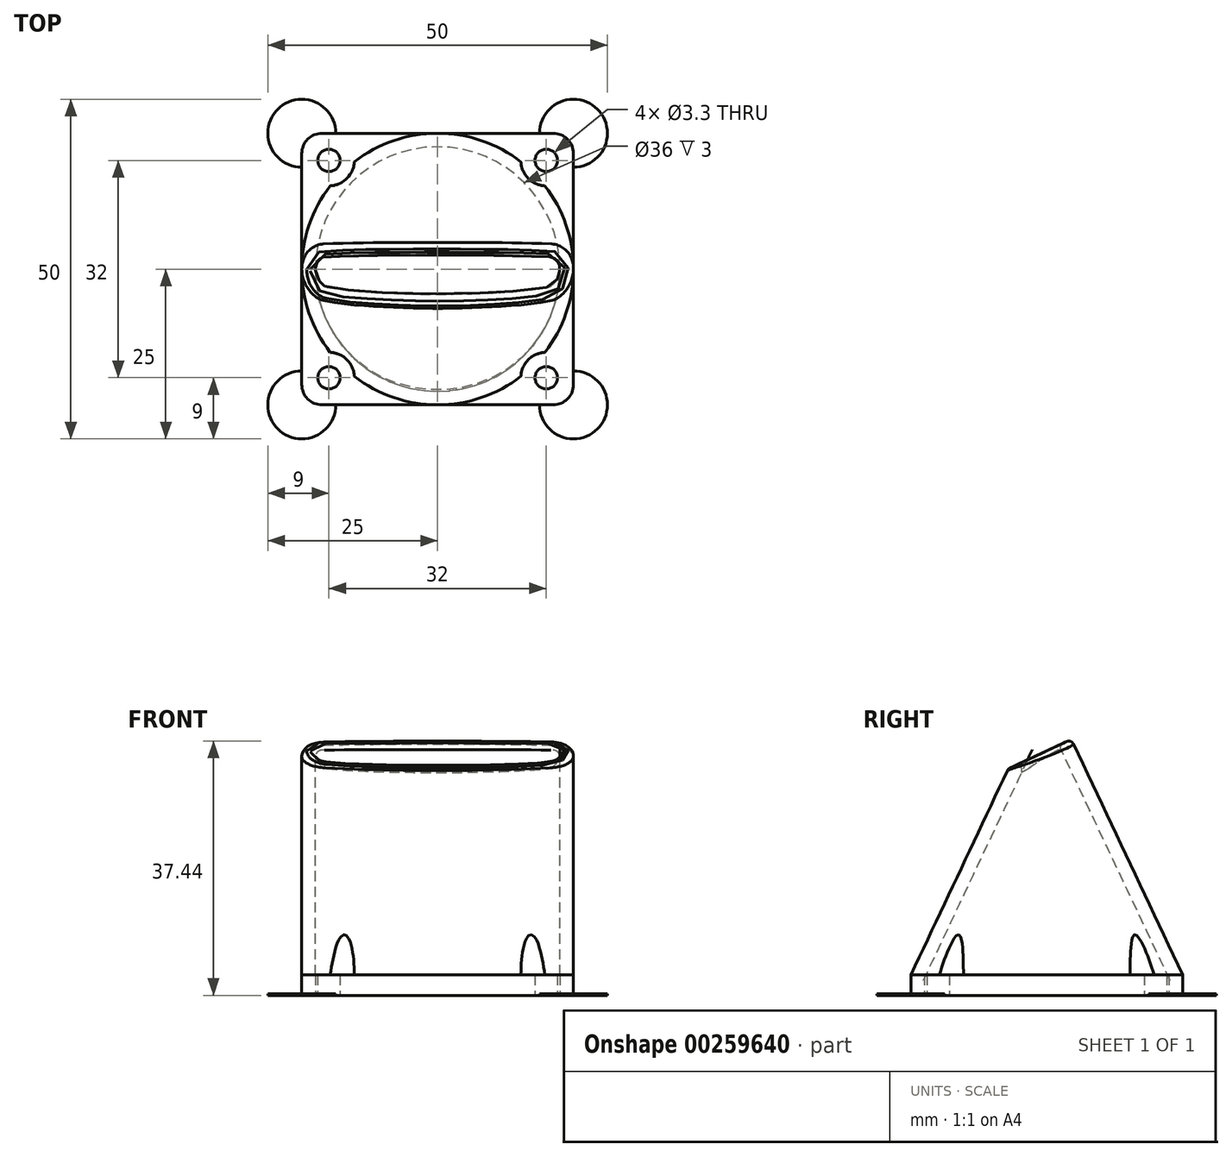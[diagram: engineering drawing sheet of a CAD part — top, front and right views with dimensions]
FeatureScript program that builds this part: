
annotation { "Feature Type Name" : "Feature", "Feature Type Description" : "" }
export const myFeature = defineFeature(function(context is Context, id is Id, definition is map)
    precondition{}
    {
        {
            var Q0;
            Q0=qCreatedBy(makeId("Top.planeOp"),FACE);
            var sketch = newSketch(context, id + "F0", { "sketchPlane" : qUnion([Q0])});
            skLineSegment(sketch, "E0.bottom", {"start": v(3, 0) * mm, "end": v(37, 0) * mm});
            skLineSegment(sketch, "E0.top", {"start": v(3, -40) * mm, "end": v(37, -40) * mm});
            skLineSegment(sketch, "E0.left", {"start": v(0, -3) * mm, "end": v(0, -37) * mm});
            skLineSegment(sketch, "E0.right", {"start": v(40, -3) * mm, "end": v(40, -37) * mm});
            skLineSegment(sketch, "E1", {"start": v(0, 0) * mm, "end": v(40, -40) * mm, "construction": true});
            skLineSegment(sketch, "E2", {"start": v(0, -40) * mm, "end": v(40, 0) * mm, "construction": true});
            skLineSegment(sketch, "E3", {"start": v(20, 0) * mm, "end": v(20, -40) * mm, "construction": true});
            skCircle(sketch, "E4", {"center": v(20, -20) * mm, "radius": 18 * mm});
            skCircle(sketch, "E5", {"center": v(4, -4) * mm, "radius": 1.65 * mm});
            skCircle(sketch, "E6", {"center": v(36, -4) * mm, "radius": 1.65 * mm});
            skCircle(sketch, "E7", {"center": v(36, -36) * mm, "radius": 1.65 * mm});
            skCircle(sketch, "E8", {"center": v(4, -36) * mm, "radius": 1.65 * mm});
            skPoint(sketch, "E9.visualSharp", {"position": v(0, -40) * mm});
            skArc(sketch, "E9.filletArc", {"start": v(0, -37) * mm, "mid": v(0.88, -39.12) * mm, "end": v(3, -40) * mm});
            skPoint(sketch, "E10.visualSharp", {"position": v(40, -40) * mm});
            skArc(sketch, "E10.filletArc", {"start": v(37, -40) * mm, "mid": v(39.12, -39.12) * mm, "end": v(40, -37) * mm});
            skPoint(sketch, "E11.visualSharp", {"position": v(40, 0) * mm});
            skArc(sketch, "E11.filletArc", {"start": v(40, -3) * mm, "mid": v(39.12, -0.88) * mm, "end": v(37, 0) * mm});
            skPoint(sketch, "E12.visualSharp", {"position": v(0, 0) * mm});
            skArc(sketch, "E12.filletArc", {"start": v(3, 0) * mm, "mid": v(0.88, -0.88) * mm, "end": v(0, -3) * mm});
            skSolve(sketch);
        }
        {
            var Q0;
            Q0=qSketchRegion(id+"F0",true);
            extrude(context, id + "F1", {"entities" : qUnion([Q0]), "depth" : 3 * mm});
        }
        {
            var Q0;
            Q0=makeQuery(id+"F1.opExtrude","CAP_FACE",FACE,{"disambiguationData":[OSD([sQuery(id+"F0.wireOp",EDGE,"E0.bottom"),sQuery(id+"F0.wireOp",EDGE,"E0.top"),sQuery(id+"F0.wireOp",EDGE,"E0.left"),sQuery(id+"F0.wireOp",EDGE,"E0.right"),sQuery(id+"F0.wireOp",EDGE,"E4"),sQuery(id+"F0.wireOp",EDGE,"E5"),sQuery(id+"F0.wireOp",EDGE,"E6"),sQuery(id+"F0.wireOp",EDGE,"E7"),sQuery(id+"F0.wireOp",EDGE,"E8"),sQuery(id+"F0.wireOp",EDGE,"E9.filletArc"),sQuery(id+"F0.wireOp",EDGE,"E10.filletArc"),sQuery(id+"F0.wireOp",EDGE,"E11.filletArc"),sQuery(id+"F0.wireOp",EDGE,"E12.filletArc")])],"isStart":false});
            var sketch = newSketch(context, id + "F2", { "sketchPlane" : qUnion([Q0])});
            skLineSegment(sketch, "E13", {"start": v(0, 0) * mm, "end": v(20, -20) * mm, "construction": true});
            skLineSegment(sketch, "E14", {"start": v(4, -36) * mm, "end": v(36, -4) * mm, "construction": true});
            skLineSegment(sketch, "E15", {"start": v(20, -20) * mm, "end": v(36, -36) * mm, "construction": true});
            skArc(sketch, "E16", {"start": v(5.86, -5.86) * mm, "mid": v(1.52, -12.35) * mm, "end": v(0, -20) * mm});
            skArc(sketch, "E17", {"start": v(5.86, -34.14) * mm, "mid": v(20, -40) * mm, "end": v(34.14, -34.14) * mm});
            skArc(sketch, "E18", {"start": v(34.14, -5.86) * mm, "mid": v(20, 0) * mm, "end": v(5.86, -5.86) * mm});
            skArc(sketch, "E19", {"start": v(34.14, -34.14) * mm, "mid": v(38.48, -27.65) * mm, "end": v(40, -20) * mm});
            skLineSegment(sketch, "E20", {"start": v(0, -20) * mm, "end": v(40, -20) * mm, "construction": true});
            skArc(sketch, "E21", {"start": v(0, -20) * mm, "mid": v(1.52, -27.65) * mm, "end": v(5.86, -34.14) * mm});
            skArc(sketch, "E22", {"start": v(40, -20) * mm, "mid": v(38.48, -12.35) * mm, "end": v(34.14, -5.86) * mm});
            skSolve(sketch);
        }
        {
            var Q0;
            Q0=makeQuery(id+"F2.imprint","IMPRINT",FACE,{"disambiguationData":[TD([[makeQuery(id+"F2.imprint","IMPRINT",EDGE,{"derivedFrom":makeQuery(id+"F1.opExtrude","CAP_EDGE",EDGE,{"disambiguationData":[OSD([sQuery(id+"F0.wireOp",EDGE,"E6")])],"isStart":false})}),-1.0]])]});
            cPlane(context, id + "F3", {"entities" : qUnion([Q0]), "cplaneType" : CPlaneType.OFFSET, "offset" : 36 * mm, "width" : 150 * mm, "height" : 150 * mm});
        }
        {
            var Q0;
            Q0=qCreatedBy(id+"F3.planeOp",FACE);
            var sketch = newSketch(context, id + "F4", { "sketchPlane" : qUnion([Q0])});
            skLineSegment(sketch, "E23", {"start": v(20, -20) * mm, "end": v(40, -20) * mm, "construction": true});
            skArc(sketch, "E24", {"start": v(3, -17) * mm, "mid": v(0.88, -17.88) * mm, "end": v(0, -20) * mm});
            skArc(sketch, "E25", {"start": v(37, -23) * mm, "mid": v(39.12, -22.12) * mm, "end": v(40, -20) * mm});
            skLineSegment(sketch, "E26", {"start": v(3, -17) * mm, "end": v(37, -17) * mm});
            skLineSegment(sketch, "E27", {"start": v(3, -23) * mm, "end": v(37, -23) * mm});
            skLineSegment(sketch, "E28", {"start": v(0, 0) * mm, "end": v(20, -20) * mm, "construction": true});
            skLineSegment(sketch, "E29", {"start": v(0, -20) * mm, "end": v(20, -20) * mm, "construction": true});
            skArc(sketch, "E30", {"start": v(0, -20) * mm, "mid": v(0.88, -22.12) * mm, "end": v(3, -23) * mm});
            skArc(sketch, "E31", {"start": v(40, -20) * mm, "mid": v(39.12, -17.88) * mm, "end": v(37, -17) * mm});
            skSolve(sketch);
        }
        {
            var Q0;
            Q0=makeQuery(id+"F1.opExtrude","SWEPT_FACE",FACE,{"disambiguationData":[OSD([sQuery(id+"F0.wireOp",EDGE,"E0.top")])]});
            cPlane(context, id + "F5", {"entities" : qUnion([Q0]), "cplaneType" : CPlaneType.OFFSET, "offset" : 20 * mm, "oppositeDirection" : true, "width" : 150 * mm, "height" : 150 * mm});
        }
        {
            var Q0;
            Q0=qCreatedBy(id+"F5.planeOp",FACE);
            var sketch = newSketch(context, id + "F6", { "sketchPlane" : qUnion([Q0])});
            skLineSegment(sketch, "E32", {"start": v(0, 0) * mm, "end": v(0, 3) * mm, "construction": true});
            skLineSegment(sketch, "E33", {"start": v(0, 3) * mm, "end": v(0, 39) * mm});
            skLineSegment(sketch, "E34", {"start": v(0, 0) * mm, "end": v(40, 0) * mm, "construction": true});
            skLineSegment(sketch, "E35", {"start": v(40, 0) * mm, "end": v(40, 3) * mm, "construction": true});
            skLineSegment(sketch, "E36", {"start": v(40, 3) * mm, "end": v(40, 39) * mm});
            skSolve(sketch);
        }
        {
            var Q0;
            Q0=makeQuery(id+"F1.opExtrude","SWEPT_FACE",FACE,{"disambiguationData":[OSD([sQuery(id+"F0.wireOp",EDGE,"E0.right")])]});
            cPlane(context, id + "F7", {"entities" : qUnion([Q0]), "cplaneType" : CPlaneType.OFFSET, "offset" : 20 * mm, "oppositeDirection" : true, "width" : 150 * mm, "height" : 150 * mm});
        }
        {
            var Q0;
            Q0=qCreatedBy(id+"F7.planeOp",FACE);
            var sketch = newSketch(context, id + "F8", { "sketchPlane" : qUnion([Q0])});
            skLineSegment(sketch, "E37", {"start": v(0, 0) * mm, "end": v(0, 3) * mm, "construction": true});
            skLineSegment(sketch, "E38", {"start": v(0, 3) * mm, "end": v(-40, 3) * mm, "construction": true});
            skLineSegment(sketch, "E39", {"start": v(0, 3) * mm, "end": v(0, 39) * mm, "construction": true});
            skLineSegment(sketch, "E40", {"start": v(0, 39) * mm, "end": v(-17, 39) * mm, "construction": true});
            skLineSegment(sketch, "E41", {"start": v(-17, 39) * mm, "end": v(-23, 39) * mm, "construction": true});
            skLineSegment(sketch, "E42", {"start": v(-23, 39) * mm, "end": v(-23, 42) * mm, "construction": true});
            skLineSegment(sketch, "E43", {"start": v(-40, 3) * mm, "end": v(-40, 0) * mm, "construction": true});
            skLineSegment(sketch, "E44", {"start": v(-23, 39) * mm, "end": v(-40, 3) * mm});
            skLineSegment(sketch, "E45", {"start": v(-17, 39) * mm, "end": v(0, 3) * mm});
            skSolve(sketch);
        }
        {
            var Q1;
            Q1=qSketchRegion(id+"F2",true);
            var Q2;
            Q2=qSketchRegion(id+"F4",true);
            var Q3;
            Q3=sQuery(id+"F6.wireOp",EDGE,"E36");
            var Q4;
            Q4=sQuery(id+"F6.wireOp",EDGE,"E33");
            var Q5;
            Q5=sQuery(id+"F8.wireOp",EDGE,"E44");
            var Q6;
            Q6=sQuery(id+"F8.wireOp",EDGE,"E45");
            loft(context, id + "F9", {"addGuides" : true, "sheetProfilesArray" : [{ "sheetProfileEntities" : qUnion([Q1]) }, { "sheetProfileEntities" : qUnion([Q2]) }], "guidesArray" : [{ "guideEntities" : qUnion([Q3]), "guideDerivativeType" : LoftGuideDerivativeType.DEFAULT, "guideDerivativeMagnitude" : 1 }, { "guideEntities" : qUnion([Q4]), "guideDerivativeType" : LoftGuideDerivativeType.DEFAULT, "guideDerivativeMagnitude" : 1 }, { "guideEntities" : qUnion([Q5]), "guideDerivativeType" : LoftGuideDerivativeType.DEFAULT, "guideDerivativeMagnitude" : 1 }, { "guideEntities" : qUnion([Q6]), "guideDerivativeType" : LoftGuideDerivativeType.DEFAULT, "guideDerivativeMagnitude" : 1 }]});
        }
        {
            var Q0;
            Q0=makeQuery(id+"F9.opLoft","CAP_FACE",FACE,{"disambiguationData":[OSD([makeQuery(id+"F4.imprint","IMPRINT",FACE,{"disambiguationData":[TD([[makeQuery(id+"F4.imprint","IMPRINT",EDGE,{"derivedFrom":sQuery(id+"F4.wireOp",EDGE,"E24")}),1.0]])]})])],"isStart":true});
            var Q1;
            {var subQ7=sQuery(id+"F2.wireOp",EDGE,"E16");Q1=makeQuery(id+"F9.opLoft","CAP_FACE",FACE,{"disambiguationData":[OSD([makeQuery(id+"F2.imprint","IMPRINT",FACE,{"disambiguationData":[TD([[makeQuery(id+"F2.imprint","IMPRINT",EDGE,{"derivedFrom":subQ7}),1.0]])]})])],"isStart":true});}
            shell(context, id + "F10", {"entities" : qUnion([Q0, Q1]), "thickness" : 2 * mm});
        }
        {
            var Q0;
            Q0=makeQuery(id+"F1.opExtrude","SWEPT_BODY",BODY,{"disambiguationData":[OSD([sQuery(id+"F0.wireOp",EDGE,"E0.bottom"),sQuery(id+"F0.wireOp",EDGE,"E0.top"),sQuery(id+"F0.wireOp",EDGE,"E0.left"),sQuery(id+"F0.wireOp",EDGE,"E0.right"),sQuery(id+"F0.wireOp",EDGE,"E4"),sQuery(id+"F0.wireOp",EDGE,"E5"),sQuery(id+"F0.wireOp",EDGE,"E6"),sQuery(id+"F0.wireOp",EDGE,"E7"),sQuery(id+"F0.wireOp",EDGE,"E8"),sQuery(id+"F0.wireOp",EDGE,"E9.filletArc"),sQuery(id+"F0.wireOp",EDGE,"E10.filletArc"),sQuery(id+"F0.wireOp",EDGE,"E11.filletArc"),sQuery(id+"F0.wireOp",EDGE,"E12.filletArc")])]});
            var Q1;
            Q1=makeQuery(id+"F9.opLoft","SWEPT_BODY",BODY,{"disambiguationData":[OSD([makeQuery(id+"F2.imprint","IMPRINT",FACE,{"disambiguationData":[TD([[makeQuery(id+"F2.imprint","IMPRINT",EDGE,{"derivedFrom":makeQuery(id+"F1.opExtrude","CAP_EDGE",EDGE,{"disambiguationData":[OSD([sQuery(id+"F0.wireOp",EDGE,"E4")])],"isStart":false})}),1.0]])]}),makeQuery(id+"F4.imprint","IMPRINT",FACE,{"disambiguationData":[TD([[makeQuery(id+"F4.imprint","IMPRINT",EDGE,{"derivedFrom":sQuery(id+"F4.wireOp",EDGE,"E24")}),1.0]])]}),sQuery(id+"F6.wireOp",EDGE,"E33"),sQuery(id+"F6.wireOp",EDGE,"E36")])]});
            booleanBodies(context, id + "F11", {"operationType" : BooleanOperationType.UNION, "tools" : qUnion([Q0, Q1])});
        }
        {
            var Q0;
            Q0=qCreatedBy(makeId("Right.planeOp"),FACE);
            var sketch = newSketch(context, id + "F12", { "sketchPlane" : qUnion([Q0])});
            skLineSegment(sketch, "E46", {"start": v(0, 0) * mm, "end": v(-20, 0) * mm, "construction": true});
            skLineSegment(sketch, "E47", {"start": v(-20, 0) * mm, "end": v(-20, 36) * mm, "construction": true});
            skLineSegment(sketch, "E48", {"start": v(-20, 36) * mm, "end": v(-1.87, 44.45) * mm});
            skLineSegment(sketch, "E49", {"start": v(-1.87, 44.45) * mm, "end": v(-6.95, 55.33) * mm});
            skLineSegment(sketch, "E50", {"start": v(-6.95, 55.33) * mm, "end": v(-43.2, 38.42) * mm});
            skLineSegment(sketch, "E51", {"start": v(-43.2, 38.42) * mm, "end": v(-38.13, 27.55) * mm});
            skLineSegment(sketch, "E52", {"start": v(-38.13, 27.55) * mm, "end": v(-20, 36) * mm});
            skSolve(sketch);
        }
        {
            var Q0;
            Q0=qSketchRegion(id+"F12",true);
            extrude(context, id + "F13", {"entities" : qUnion([Q0]), "operationType" : NewBodyOperationType.REMOVE, "endBound" : BoundingType.THROUGH_ALL, "depth" : 25 * mm});
        }
        {
            var Q0;
            Q0=makeQuery(id+"F13.boolean.opBoolean","INTERSECT",EDGE,{"derivedFrom":[makeQuery(id+"F10.opShell","OFFSET_FACE",FACE,{"disambiguationData":[OSD([sQuery(id+"F2.wireOp",EDGE,"E16"),sQuery(id+"F2.wireOp",EDGE,"E17"),sQuery(id+"F2.wireOp",EDGE,"E21"),sQuery(id+"F4.wireOp",EDGE,"E30"),sQuery(id+"F6.wireOp",EDGE,"E33")])]}),makeQuery(id+"F13.opExtrude","SWEPT_FACE",FACE,{"disambiguationData":[OSD([sQuery(id+"F12.wireOp",EDGE,"E48"),sQuery(id+"F12.wireOp",EDGE,"E52")])]})]});
            var Q1;
            Q1=makeQuery(id+"F13.boolean.opBoolean","INTERSECT",EDGE,{"derivedFrom":[makeQuery(id+"F9.opLoft","SWEPT_FACE",FACE,{"disambiguationData":[OSD([sQuery(id+"F2.wireOp",EDGE,"E16"),sQuery(id+"F2.wireOp",EDGE,"E17"),sQuery(id+"F2.wireOp",EDGE,"E21"),sQuery(id+"F4.wireOp",EDGE,"E30"),sQuery(id+"F6.wireOp",EDGE,"E33")])]}),makeQuery(id+"F13.opExtrude","SWEPT_FACE",FACE,{"disambiguationData":[OSD([sQuery(id+"F12.wireOp",EDGE,"E48"),sQuery(id+"F12.wireOp",EDGE,"E52")])]})]});
            fillet(context, id + "F14", {"entities" : qUnion([Q0, Q1]), "radius" : 0.75 * mm, "tangentPropagation" : true, "allowEdgeOverflow" : false});
        }
        {
            var Q0;
            Q0=qCreatedBy(makeId("Top.planeOp"),FACE);
            var sketch = newSketch(context, id + "F15", { "sketchPlane" : qUnion([Q0])});
            skLineSegment(sketch, "E53.bottom", {"start": v(0, 0) * mm, "end": v(40, 0) * mm, "construction": true});
            skLineSegment(sketch, "E53.top", {"start": v(0, -40) * mm, "end": v(40, -40) * mm, "construction": true});
            skLineSegment(sketch, "E53.left", {"start": v(0, 0) * mm, "end": v(0, -40) * mm, "construction": true});
            skLineSegment(sketch, "E53.right", {"start": v(40, 0) * mm, "end": v(40, -40) * mm, "construction": true});
            skLineSegment(sketch, "E54", {"start": v(0, 0) * mm, "end": v(40, -40) * mm, "construction": true});
            skLineSegment(sketch, "E55", {"start": v(0, -40) * mm, "end": v(40, 0) * mm, "construction": true});
            skLineSegment(sketch, "E56", {"start": v(20, 0) * mm, "end": v(20, -40) * mm, "construction": true});
            skArc(sketch, "E57", {"start": v(4.39, -2.4) * mm, "mid": v(2.83, -2.83) * mm, "end": v(2.4, -4.39) * mm});
            skArc(sketch, "E58", {"start": v(4.39, -2.4) * mm, "mid": v(-3.54, 3.54) * mm, "end": v(2.4, -4.39) * mm});
            skArc(sketch, "E59", {"start": v(37.6, -4.39) * mm, "mid": v(37.17, -2.83) * mm, "end": v(35.61, -2.4) * mm});
            skArc(sketch, "E60", {"start": v(37.6, -4.39) * mm, "mid": v(43.54, 3.54) * mm, "end": v(35.61, -2.4) * mm});
            skArc(sketch, "E61", {"start": v(35.61, -37.6) * mm, "mid": v(43.54, -43.54) * mm, "end": v(37.6, -35.61) * mm});
            skArc(sketch, "E62", {"start": v(35.61, -37.6) * mm, "mid": v(37.17, -37.17) * mm, "end": v(37.6, -35.61) * mm});
            skArc(sketch, "E63", {"start": v(2.4, -35.61) * mm, "mid": v(-3.54, -43.54) * mm, "end": v(4.39, -37.6) * mm});
            skArc(sketch, "E64", {"start": v(2.4, -35.61) * mm, "mid": v(2.83, -37.17) * mm, "end": v(4.39, -37.6) * mm});
            skSolve(sketch);
        }
        {
            var Q0;
            Q0=qSketchRegion(id+"F15",true);
            extrude(context, id + "F16", {"entities" : qUnion([Q0]), "operationType" : NewBodyOperationType.ADD, "depth" : 0.2 * mm});
        }
        {
            var Q0;
            {var subQ0=sQuery(id+"F0.wireOp",EDGE,"E0.right");var subQ1=sQuery(id+"F0.wireOp",EDGE,"E10.filletArc");var subQ2=sQuery(id+"F0.wireOp",EDGE,"E7");var subQ3=sQuery(id+"F0.wireOp",EDGE,"E0.top");var subQ4=makeQuery(id+"F1.opExtrude","CAP_FACE",FACE,{"disambiguationData":[OSD([sQuery(id+"F0.wireOp",EDGE,"E0.bottom"),subQ3,sQuery(id+"F0.wireOp",EDGE,"E0.left"),subQ0,sQuery(id+"F0.wireOp",EDGE,"E4"),sQuery(id+"F0.wireOp",EDGE,"E5"),sQuery(id+"F0.wireOp",EDGE,"E6"),subQ2,sQuery(id+"F0.wireOp",EDGE,"E8"),sQuery(id+"F0.wireOp",EDGE,"E9.filletArc"),subQ1,sQuery(id+"F0.wireOp",EDGE,"E11.filletArc"),sQuery(id+"F0.wireOp",EDGE,"E12.filletArc")])],"isStart":false});Q0=makeQuery(id+"F11.opBoolean","SPLIT",FACE,{"disambiguationData":[TD([makeQuery(id+"F1.opExtrude","SWEPT_FACE",FACE,{"disambiguationData":[OSD([subQ2])]})])],"derivedFrom":subQ4});}
            var sketch = newSketch(context, id + "F17", { "sketchPlane" : qUnion([Q0])});
            skCircle(sketch, "E65", {"center": v(36, -36) * mm, "radius": 3.75 * mm});
            skLineSegment(sketch, "E66.bottom", {"start": v(36, -36) * mm, "end": v(4, -36) * mm, "construction": true});
            skLineSegment(sketch, "E66.top", {"start": v(36, -4) * mm, "end": v(4, -4) * mm, "construction": true});
            skLineSegment(sketch, "E66.left", {"start": v(36, -36) * mm, "end": v(36, -4) * mm, "construction": true});
            skLineSegment(sketch, "E66.right", {"start": v(4, -36) * mm, "end": v(4, -4) * mm, "construction": true});
            skCircle(sketch, "E67", {"center": v(4, -36) * mm, "radius": 3.75 * mm});
            skCircle(sketch, "E68", {"center": v(4, -4) * mm, "radius": 3.75 * mm});
            skCircle(sketch, "E69", {"center": v(36, -4) * mm, "radius": 3.75 * mm});
            skSolve(sketch);
        }
        {
            var Q0;
            Q0=qSketchRegion(id+"F17",true);
            extrude(context, id + "F18", {"entities" : qUnion([Q0]), "operationType" : NewBodyOperationType.REMOVE, "depth" : 25 * mm});
        }
    });
